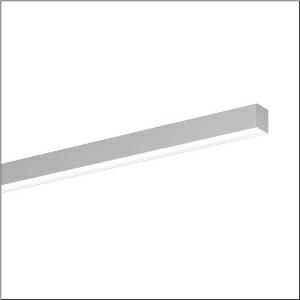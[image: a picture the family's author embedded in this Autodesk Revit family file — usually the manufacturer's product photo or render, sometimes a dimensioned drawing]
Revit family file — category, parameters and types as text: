
# Revit family: silica_21_51mx23da34sb
name_source: partatom
category: Lighting Fixtures
units: mm (PartAtom-declared; Revit-internal decimal feet)

## family parameters
Cut with Voids When Loaded = No
Host = Face
Light Source = No
Part Type = Normal
Room Calculation Point = No
Round Connector Dimension = Use Diameter
Shared = No

## types (1)
- --- (1 x LED, 3280 lm, 24.1 W, 3000K)
    Apparent Load = 24 VA
    CIE Flux Codes = 78 96 99 100 100
    Color Rendering = 80
    Color Temperature = 3000K
    Default Elevation = 1800 mm
    Description = Silica 21, office luminaire, primary optical cover: prismatic diffuser, of PMMA, CAT 2 (L<= 3000cd/m²), light emission: direct distribution, primary light characteristic: symmetric, installation type: surface-mounted, LED, rated luminous flux: 3.280lm, luminous efficacy: 136lm/W, light colour: 830, colour temperature: 3000K, control gear: DALI 2, with terminal, 3+2-pole, max. 2.5mm², mains connection: 220..240V, AC, 50/60Hz, rated input power: 24.1W, luminaire housing, of aluminium, metallic grey (RAL 9006), length: 1.204mm, width: 53mm, height: 53mm, protection rating (complete): IP20, insulation class (complete): insulation class I (protective earthing), certification: CE, permissible operating ambient temperature: 0..+35°C, standard: EN 50419, packaging unit: 1 piece
    Height = 53 mm
    Lamp = 1 x LED
    Lamp Light Flux = 3280 lm
    Lamp Power = 24.1 W
    Lamp count = 1
    Length = 1204 mm
    Luminous efficacy = 136 lm/W
    Manufacturer = Siteco
    ModVariant = No
    Model = 51MX23DA34SB
    Mounting Place = Ceiling
    Mounting Type = Surface mounted
    Number of Poles = 1
    OnlyDefault = Yes
    Power Factor = 1
    Product Name = Silica 21
    Product group = office luminaire | ceiling mounted
    ProductGroupID = 301
    Protection Class = Protection class I
    Protection Degree = IP 20
    RLX_Detail_Level = 1
    RLX_Emergency_Light_Flux = 0 lm
    RLX_Emergency_Type = 0
    RLX_Emergency_Type_DB = No
    RlxData = <blob elided: 21249 chars, md5=a3708fe3>
    Socket = socket
    Standby Power = 0 W
    System Light Flux = 3280 lm
    System Power = 24 W
    Type Comments = factory setting: luminous flux: 100 % | dim-lin: 254 | 345 mA
    Type Image = l_1335933.jpg
    URL = http://relux.com
    VarID = @adj_028077
    Voltage = 0 V
    Weight = 0.00 kg
    Width = 53 mm

## geometry (parser evidence)
native form markers: Blend x4, Sweep x10
no freeform markers — native parametric forms only
